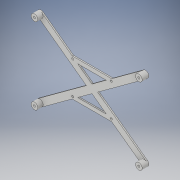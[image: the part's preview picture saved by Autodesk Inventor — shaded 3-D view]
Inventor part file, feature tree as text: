
AUTODESK INVENTOR PART (.ipt)
format: ipt  version: 2018 (Build 220112000, 112)  size: 180,736 bytes
history: native  units: in
note: dims shown in document units (in); Inventor stores cm internally (conversion verified against a paired STEP export)
features: extrude x5, sketch x4
ambient origin geometry x8: Origin, YZ Plane, XZ Plane, XY Plane, X Axis, Y Axis, Z Axis, Center Point
bodies: Body1 (feature_tree)
feature tree (9):
  extrude  "Extrusion3"  Depth=5.2862in
  extrude  "Extrusion4"  Depth=3.5039in
  extrude  "Extrusion5"  Depth=0.1181in
  sketch  "Sketch5"  dims[d6=6.1772in d7=0.3543in d17=0.5906in d18=0.5472in d19=0.3937in d20=0.0787in d21=0.0in d22=0.315in d23=0.0in d24=0.122in d25=0.315in d26=0.0in d27=2.2835in d28=1.9291in d29=0.122in d30=0.2362in d31=0.0984in d32=0.3937in d33=0.0in d34=0.3937in d35=0.0in]
  extrude  "Extrusion6"  Depth=0.3937in
  extrude  "Extrusion7"  Depth=0.3937in
  sketch  "Sketch1"  dims[d0=7.2795in d1=5.2862in]
  sketch  "Sketch3"  dims[d2=6.1417in d3=3.5039in]
  sketch  "Sketch4"  dims[d4=4.526in d5=0.1181in]
